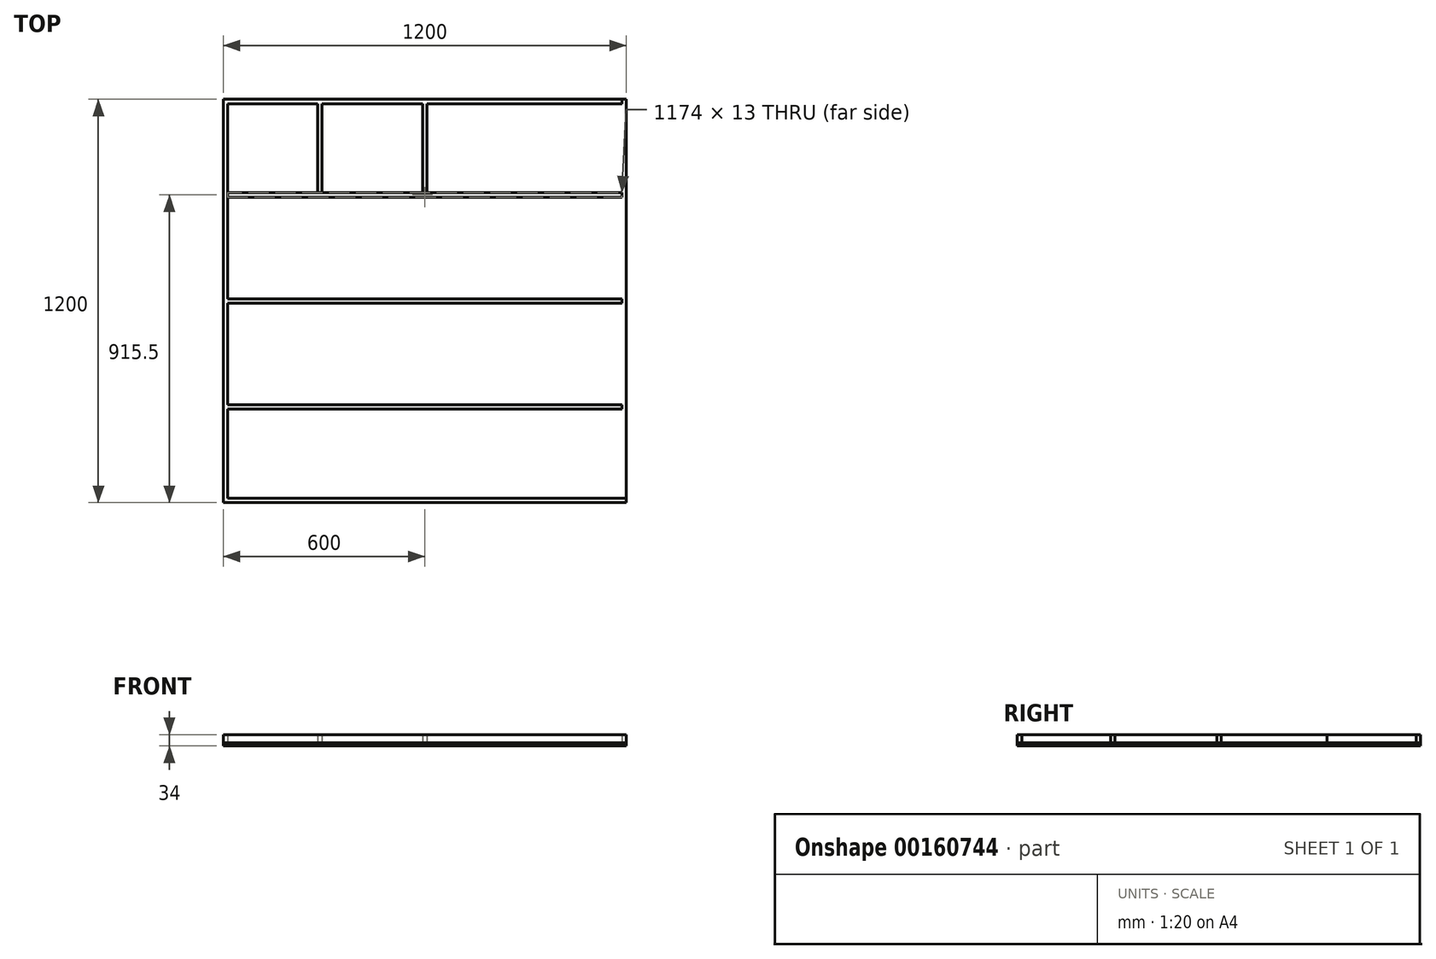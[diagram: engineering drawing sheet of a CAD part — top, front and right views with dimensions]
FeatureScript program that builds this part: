
annotation { "Feature Type Name" : "Feature", "Feature Type Description" : "" }
export const myFeature = defineFeature(function(context is Context, id is Id, definition is map)
    precondition{}
    {
        {
            var Q0;
            Q0=qCreatedBy(makeId("Top.planeOp"),FACE);
            var sketch = newSketch(context, id + "F0", { "sketchPlane" : qUnion([Q0])});
            skLineSegment(sketch, "E0.bottom", {"start": v(0, 0) * mm, "end": v(1200, 0) * mm});
            skLineSegment(sketch, "E0.top", {"start": v(0, -1200) * mm, "end": v(1200, -1200) * mm});
            skLineSegment(sketch, "E0.left", {"start": v(0, 0) * mm, "end": v(0, -1200) * mm});
            skLineSegment(sketch, "E0.right", {"start": v(1200, 0) * mm, "end": v(1200, -1200) * mm});
            skLineSegment(sketch, "E1", {"start": v(13, -1200) * mm, "end": v(13, 0) * mm});
            skLineSegment(sketch, "E2", {"start": v(13, -1187) * mm, "end": v(1200, -1187) * mm});
            skLineSegment(sketch, "E3", {"start": v(1187, 0) * mm, "end": v(1187, -1187) * mm});
            skLineSegment(sketch, "E4", {"start": v(13, -13) * mm, "end": v(1187, -13) * mm});
            skLineSegment(sketch, "E5", {"start": v(13, -278) * mm, "end": v(1187, -278) * mm});
            skLineSegment(sketch, "E6", {"start": v(1187, -278) * mm, "end": v(1187, -291) * mm});
            skLineSegment(sketch, "E7", {"start": v(1187, -291) * mm, "end": v(13, -291) * mm});
            skLineSegment(sketch, "E8", {"start": v(13, -593.5) * mm, "end": v(1187, -593.5) * mm});
            skLineSegment(sketch, "E9", {"start": v(13, -606.5) * mm, "end": v(1187, -606.5) * mm});
            skLineSegment(sketch, "E10", {"start": v(0, -600) * mm, "end": v(1200, -600) * mm, "construction": true});
            skLineSegment(sketch, "E11", {"start": v(13, -909) * mm, "end": v(1187, -909) * mm});
            skLineSegment(sketch, "E12", {"start": v(13, -922) * mm, "end": v(1187, -922) * mm});
            skLineSegment(sketch, "E13", {"start": v(593.8, -13) * mm, "end": v(593.8, -278) * mm});
            skLineSegment(sketch, "E14", {"start": v(606.8, -13) * mm, "end": v(606.8, -278) * mm});
            skLineSegment(sketch, "E15", {"start": v(600, 0) * mm, "end": v(600, -1200) * mm, "construction": true});
            skLineSegment(sketch, "E16", {"start": v(280.8, -13) * mm, "end": v(280.8, -278) * mm});
            skLineSegment(sketch, "E17", {"start": v(293.8, -13) * mm, "end": v(293.8, -278) * mm});
            skSolve(sketch);
        }
        {
            var Q0;
            Q0 = qSketchRegion(id + "F0", true);
            var Q1;
            {var subQ3=sQuery(id+"F0.wireOp",EDGE,"E12");Q1=makeQuery(id+"F0.imprint","IMPRINT",FACE,{"disambiguationData":[TD([[makeQuery(id+"F0.imprint","IMPRINT",EDGE,{"derivedFrom":subQ3}),-1.0]])]});}
            var Q2;
            {var subQ0=sQuery(id+"F0.wireOp",EDGE,"E9");Q2=makeQuery(id+"F0.imprint","IMPRINT",FACE,{"disambiguationData":[TD([[makeQuery(id+"F0.imprint","IMPRINT",EDGE,{"derivedFrom":subQ0}),-1.0]])]});}
            var Q3;
            {var subQ0=sQuery(id+"F0.wireOp",EDGE,"E7");Q3=makeQuery(id+"F0.imprint","IMPRINT",FACE,{"disambiguationData":[TD([[makeQuery(id+"F0.imprint","IMPRINT",EDGE,{"derivedFrom":subQ0}),1.0]])]});}
            var Q4;
            {var subQ5=sQuery(id+"F0.wireOp",EDGE,"E16");Q4=makeQuery(id+"F0.imprint","IMPRINT",FACE,{"disambiguationData":[TD([[makeQuery(id+"F0.imprint","IMPRINT",EDGE,{"derivedFrom":subQ5}),-1.0]])]});}
            var Q5;
            {var subQ0=sQuery(id+"F0.wireOp",EDGE,"E13");Q5=makeQuery(id+"F0.imprint","IMPRINT",FACE,{"disambiguationData":[TD([[makeQuery(id+"F0.imprint","IMPRINT",EDGE,{"derivedFrom":subQ0}),-1.0]])]});}
            var Q6;
            {var subQ5=sQuery(id+"F0.wireOp",EDGE,"E14");Q6=makeQuery(id+"F0.imprint","IMPRINT",FACE,{"disambiguationData":[TD([[makeQuery(id+"F0.imprint","IMPRINT",EDGE,{"derivedFrom":subQ5}),1.0]])]});}
            var Q7;
            {var subQ0=sQuery(id+"F0.wireOp",EDGE,"E16");Q7=makeQuery(id+"F0.imprint","IMPRINT",FACE,{"disambiguationData":[TD([[makeQuery(id+"F0.imprint","IMPRINT",EDGE,{"derivedFrom":subQ0}),1.0]])]});}
            var Q8;
            {var subQ8=sQuery(id+"F0.wireOp",EDGE,"E6");Q8=makeQuery(id+"F0.imprint","IMPRINT",FACE,{"disambiguationData":[TD([[makeQuery(id+"F0.imprint","IMPRINT",EDGE,{"derivedFrom":subQ8}),-1.0]])]});}
            var Q9;
            {var subQ0=sQuery(id+"F0.wireOp",EDGE,"E13");Q9=makeQuery(id+"F0.imprint","IMPRINT",FACE,{"disambiguationData":[TD([[makeQuery(id+"F0.imprint","IMPRINT",EDGE,{"derivedFrom":subQ0}),1.0]])]});}
            var Q10;
            {var subQ0=sQuery(id+"F0.wireOp",EDGE,"E8");Q10=makeQuery(id+"F0.imprint","IMPRINT",FACE,{"disambiguationData":[TD([[makeQuery(id+"F0.imprint","IMPRINT",EDGE,{"derivedFrom":subQ0}),-1.0]])]});}
            var Q11;
            {var subQ0=sQuery(id+"F0.wireOp",EDGE,"E11");Q11=makeQuery(id+"F0.imprint","IMPRINT",FACE,{"disambiguationData":[TD([[makeQuery(id+"F0.imprint","IMPRINT",EDGE,{"derivedFrom":subQ0}),-1.0]])]});}
            extrude(context, id + "F1", {"entities" : qUnion([Q0, Q1, Q2, Q3, Q4, Q5, Q6, Q7, Q8, Q9, Q10, Q11]), "depth" : 10 * mm});
        }
        {
            var Q0;
            {var subQ11=sQuery(id+"F0.wireOp",EDGE,"E0.left");Q0=makeQuery(id+"F0.imprint","IMPRINT",FACE,{"disambiguationData":[TD([[makeQuery(id+"F0.imprint","IMPRINT",EDGE,{"derivedFrom":subQ11}),1.0]])]});}
            var Q1;
            {var subQ0=sQuery(id+"F0.wireOp",EDGE,"E11");Q1=makeQuery(id+"F0.imprint","IMPRINT",FACE,{"disambiguationData":[TD([[makeQuery(id+"F0.imprint","IMPRINT",EDGE,{"derivedFrom":subQ0}),-1.0]])]});}
            var Q2;
            {var subQ4=sQuery(id+"F0.wireOp",EDGE,"E0.top");var subQ6=sQuery(id+"F0.wireOp",EDGE,"E0.right");var subQ7=makeQuery(id+"F0.imprint","INTERSECT",VERTEX,{"derivedFrom":[subQ4,subQ6]});Q2=makeQuery(id+"F0.imprint","IMPRINT",FACE,{"disambiguationData":[TD([[makeQuery(id+"F0.imprint","IMPRINT",EDGE,{"disambiguationData":[TD([[subQ7,1.0]])],"derivedFrom":subQ4}),1.0]])]});}
            var Q3;
            {var subQ0=sQuery(id+"F0.wireOp",EDGE,"E6");Q3=makeQuery(id+"F0.imprint","IMPRINT",FACE,{"disambiguationData":[TD([[makeQuery(id+"F0.imprint","IMPRINT",EDGE,{"derivedFrom":subQ0}),1.0]])]});}
            var Q4;
            {var subQ0=sQuery(id+"F0.wireOp",EDGE,"E8");Q4=makeQuery(id+"F0.imprint","IMPRINT",FACE,{"disambiguationData":[TD([[makeQuery(id+"F0.imprint","IMPRINT",EDGE,{"derivedFrom":subQ0}),-1.0]])]});}
            var Q5;
            {var subQ8=sQuery(id+"F0.wireOp",EDGE,"E6");Q5=makeQuery(id+"F0.imprint","IMPRINT",FACE,{"disambiguationData":[TD([[makeQuery(id+"F0.imprint","IMPRINT",EDGE,{"derivedFrom":subQ8}),-1.0]])]});}
            var Q6;
            {var subQ0=sQuery(id+"F0.wireOp",EDGE,"E13");Q6=makeQuery(id+"F0.imprint","IMPRINT",FACE,{"disambiguationData":[TD([[makeQuery(id+"F0.imprint","IMPRINT",EDGE,{"derivedFrom":subQ0}),1.0]])]});}
            var Q7;
            {var subQ0=sQuery(id+"F0.wireOp",EDGE,"E16");Q7=makeQuery(id+"F0.imprint","IMPRINT",FACE,{"disambiguationData":[TD([[makeQuery(id+"F0.imprint","IMPRINT",EDGE,{"derivedFrom":subQ0}),1.0]])]});}
            var Q8;
            {var subQ1=sQuery(id+"F0.wireOp",EDGE,"E1");var subQ5=sQuery(id+"F0.wireOp",EDGE,"E0.bottom");var subQ8=makeQuery(id+"F0.imprint","INTERSECT",VERTEX,{"derivedFrom":[subQ5,subQ1]});Q8=makeQuery(id+"F0.imprint","IMPRINT",FACE,{"disambiguationData":[TD([[makeQuery(id+"F0.imprint","IMPRINT",EDGE,{"disambiguationData":[TD([[subQ8,-1.0]])],"derivedFrom":subQ5}),-1.0]])]});}
            extrude(context, id + "F2", {"entities" : qUnion([Q0, Q1, Q2, Q3, Q4, Q5, Q6, Q7, Q8]), "depth" : 34 * mm, "hasSecondDirection" : true, "secondDirectionOppositeDirection" : false, "secondDirectionDepth" : 10 * mm});
        }
    });
